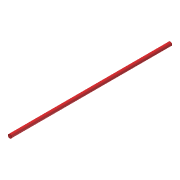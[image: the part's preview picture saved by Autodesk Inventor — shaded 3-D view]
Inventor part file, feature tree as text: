
AUTODESK INVENTOR PART (.ipt)
format: ipt  version: 2012 (Build 160160000, 160)  size: 64,512 bytes
history: native  units: in
note: dims shown in document units (in); Inventor stores cm internally (conversion verified against a paired STEP export)
features: extrude x1, sketch x1
ambient origin geometry x8: Origin, YZ Plane, XZ Plane, XY Plane, X Axis, Y Axis, Z Axis, Center Point
bodies: Solid1 (feature_tree)
feature tree (2):
  extrude  "Extrusion1"  Depth=11.0in TaperAngle=0.0deg
  sketch  "Sketch1"  dims[d0=0.25in d1=11.0in d2=0.0in]
